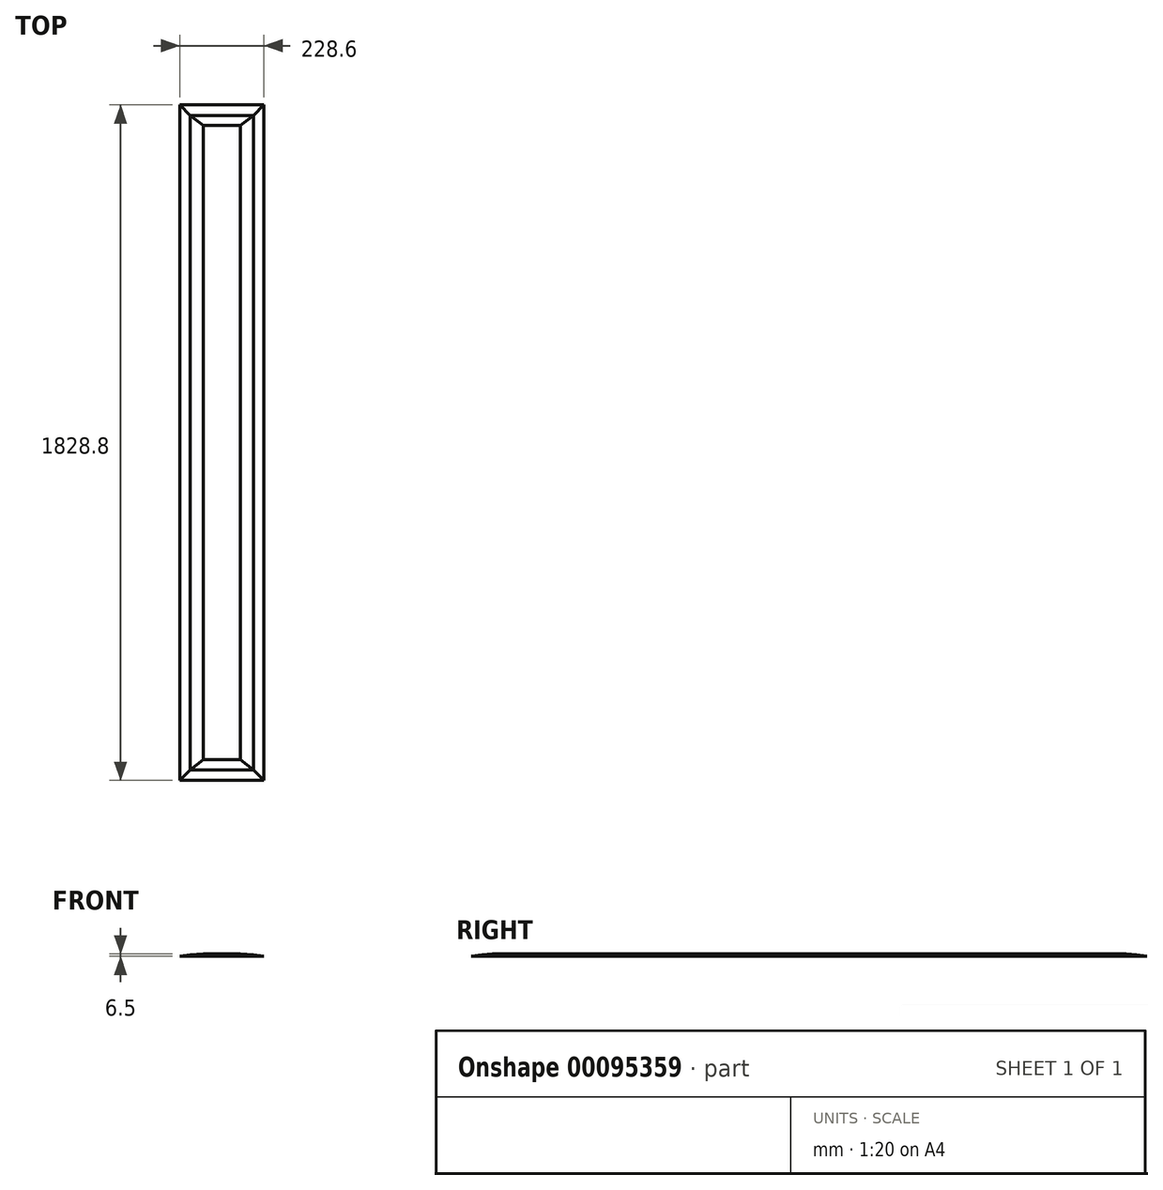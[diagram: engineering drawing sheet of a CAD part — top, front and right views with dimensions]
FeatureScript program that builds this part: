
annotation { "Feature Type Name" : "Feature", "Feature Type Description" : "" }
export const myFeature = defineFeature(function(context is Context, id is Id, definition is map)
    precondition{}
    {
        {
            var Q0;
            Q0=qCreatedBy(makeId("Top.planeOp"),FACE);
            var sketch = newSketch(context, id + "F0", { "sketchPlane" : qUnion([Q0])});
            skLineSegment(sketch, "E0.bottom", {"start": v(-114.3, 914.4) * mm, "end": v(114.3, 914.4) * mm});
            skLineSegment(sketch, "E0.top", {"start": v(-114.3, -914.4) * mm, "end": v(114.3, -914.4) * mm});
            skLineSegment(sketch, "E0.left", {"start": v(-114.3, 914.4) * mm, "end": v(-114.3, -914.4) * mm});
            skLineSegment(sketch, "E0.right", {"start": v(114.3, 914.4) * mm, "end": v(114.3, -914.4) * mm});
            skLineSegment(sketch, "E1", {"start": v(-114.3, 914.4) * mm, "end": v(0, 0) * mm, "construction": true});
            skLineSegment(sketch, "E2", {"start": v(-114.3, -914.4) * mm, "end": v(114.3, 914.4) * mm, "construction": true});
            skLineSegment(sketch, "E3", {"start": v(0, 0) * mm, "end": v(114.3, -914.4) * mm, "construction": true});
            skSolve(sketch);
        }
        {
            assignVariable(context, id + "F1", {"name" : "HeightStop", "anyValue" : 6.5});
        }
        {
            var Q0;
            Q0=makeQuery(id+"F0.imprint","IMPRINT",FACE,{"disambiguationData":[TD([[makeQuery(id+"F0.imprint","IMPRINT",EDGE,{"derivedFrom":sQuery(id+"F0.wireOp",EDGE,"E0.bottom")}),-1.0]])]});
            cPlane(context, id + "F2", {"entities" : qUnion([Q0]), "cplaneType" : CPlaneType.OFFSET, "offset" : (2 / 3 * getVariable(context, 'HeightStop')) * mm, "width" : 152.4 * mm, "height" : 152.4 * mm});
        }
        {
            var Q0;
            Q0=qCreatedBy(id+"F2.planeOp",FACE);
            var sketch = newSketch(context, id + "F3", { "sketchPlane" : qUnion([Q0])});
            skLineSegment(sketch, "E4.bottom", {"start": v(-85.72, 885.82) * mm, "end": v(85.73, 885.82) * mm});
            skLineSegment(sketch, "E4.top", {"start": v(-85.73, -885.83) * mm, "end": v(85.72, -885.83) * mm});
            skLineSegment(sketch, "E4.left", {"start": v(-85.72, 885.82) * mm, "end": v(-85.73, -885.83) * mm});
            skLineSegment(sketch, "E4.right", {"start": v(85.73, 885.82) * mm, "end": v(85.72, -885.83) * mm});
            skLineSegment(sketch, "E5", {"start": v(-85.72, 885.83) * mm, "end": v(0, 0) * mm});
            skLineSegment(sketch, "E6", {"start": v(85.73, 885.82) * mm, "end": v(-85.73, -885.83) * mm});
            skLineSegment(sketch, "E7", {"start": v(0, 0) * mm, "end": v(85.72, -885.83) * mm});
            skSolve(sketch);
        }
        {
            var Q0;
            Q0 = qSketchRegion(id + "F0", true);
            var Q1;
            Q1 = qSketchRegion(id + "F3", true);
            loft(context, id + "F4", {"sheetProfilesArray" : [{ "sheetProfileEntities" : qUnion([Q0]) }, { "sheetProfileEntities" : qUnion([Q1]) }]});
        }
        {
            var Q0;
            Q0=makeQuery(id+"F0.imprint","IMPRINT",FACE,{"disambiguationData":[TD([[makeQuery(id+"F0.imprint","IMPRINT",EDGE,{"derivedFrom":sQuery(id+"F0.wireOp",EDGE,"E0.bottom")}),-1.0]])]});
            cPlane(context, id + "F5", {"entities" : qUnion([Q0]), "cplaneType" : CPlaneType.OFFSET, "offset" : (getVariable(context, 'HeightStop')) * mm, "width" : 152.4 * mm, "height" : 152.4 * mm});
        }
        {
            var Q0;
            Q0=qCreatedBy(id+"F5.planeOp",FACE);
            var sketch = newSketch(context, id + "F6", { "sketchPlane" : qUnion([Q0])});
            skLineSegment(sketch, "E8.bottom", {"start": v(50.8, 858.14) * mm, "end": v(-50.8, 858.14) * mm});
            skLineSegment(sketch, "E8.top", {"start": v(50.8, -858.14) * mm, "end": v(-50.8, -858.14) * mm});
            skLineSegment(sketch, "E8.left", {"start": v(50.8, 858.14) * mm, "end": v(50.8, -858.14) * mm});
            skLineSegment(sketch, "E8.right", {"start": v(-50.8, 858.14) * mm, "end": v(-50.8, -858.14) * mm});
            skLineSegment(sketch, "E9", {"start": v(50.8, 858.14) * mm, "end": v(0, 0) * mm, "construction": true});
            skLineSegment(sketch, "E10", {"start": v(50.8, -858.14) * mm, "end": v(-50.8, 858.14) * mm, "construction": true});
            skLineSegment(sketch, "E11", {"start": v(0, 0) * mm, "end": v(-50.8, -858.14) * mm, "construction": true});
            skSolve(sketch);
        }
        {
            var Q1;
            {var subQ0=sQuery(id+"F3.wireOp",EDGE,"E4.right");Q1=makeQuery(id+"F4.opLoft","CAP_FACE",FACE,{"disambiguationData":[OSD([makeQuery(id+"F3.imprint","IMPRINT",FACE,{"disambiguationData":[TD([[makeQuery(id+"F3.imprint","IMPRINT",EDGE,{"derivedFrom":subQ0}),-1.0]])]})])],"isStart":true});}
            var Q2;
            Q2=makeQuery(id+"F6.imprint","IMPRINT",FACE,{"disambiguationData":[TD([[makeQuery(id+"F6.imprint","IMPRINT",EDGE,{"derivedFrom":sQuery(id+"F6.wireOp",EDGE,"E8.bottom")}),1.0]])]});
            loft(context, id + "F7", {"operationType" : NewBodyOperationType.ADD, "sheetProfilesArray" : [{ "sheetProfileEntities" : qUnion([Q1]) }, { "sheetProfileEntities" : qUnion([Q2]) }]});
        }
    });
